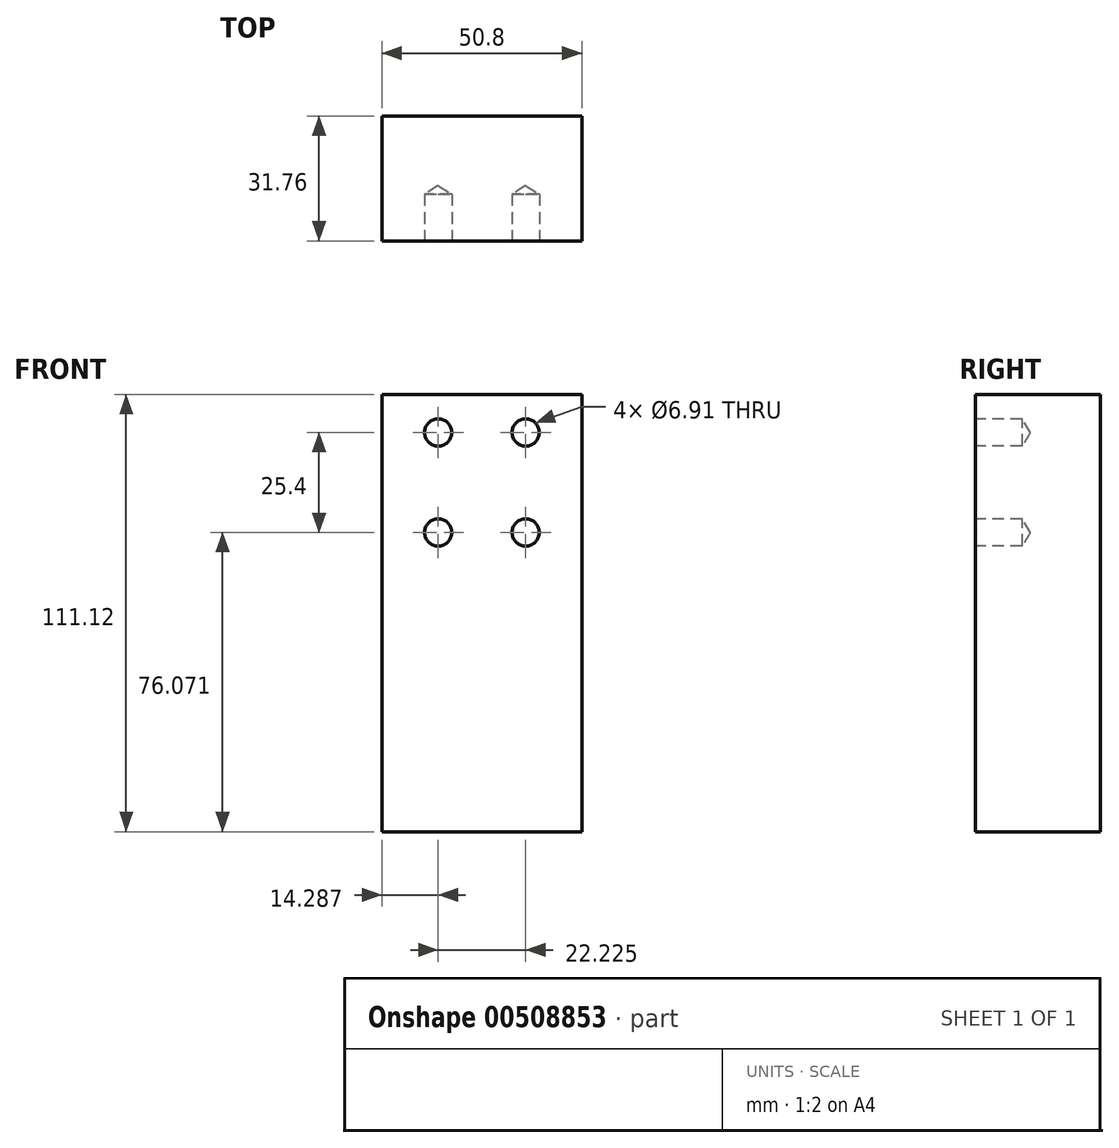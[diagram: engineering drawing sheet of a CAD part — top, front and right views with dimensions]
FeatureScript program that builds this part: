
annotation { "Feature Type Name" : "Feature", "Feature Type Description" : "" }
export const myFeature = defineFeature(function(context is Context, id is Id, definition is map)
    precondition{}
    {
        {
            var Q0;
            Q0=qCreatedBy(makeId("Front.planeOp"),FACE);
            var sketch = newSketch(context, id + "F0", { "sketchPlane" : qUnion([Q0])});
            skLineSegment(sketch, "E0.bottom", {"start": v(25.4, 55.56) * mm, "end": v(-25.4, 55.56) * mm});
            skLineSegment(sketch, "E0.top", {"start": v(25.4, -55.56) * mm, "end": v(-25.4, -55.56) * mm});
            skLineSegment(sketch, "E0.left", {"start": v(25.4, 55.56) * mm, "end": v(25.4, -55.56) * mm});
            skLineSegment(sketch, "E0.right", {"start": v(-25.4, 55.56) * mm, "end": v(-25.4, -55.56) * mm});
            skPoint(sketch, "E0.middle", {"position": v(0, 0) * mm});
            skSolve(sketch);
        }
        {
            var Q0;
            Q0=makeQuery(id+"F0.imprint","IMPRINT",FACE,{"disambiguationData":[TD([[makeQuery(id+"F0.imprint","IMPRINT",EDGE,{"derivedFrom":sQuery(id+"F0.wireOp",EDGE,"E0.bottom")}),1.0]])]});
            extrude(context, id + "F1", {"entities" : qUnion([Q0]), "endBound" : BoundingType.SYMMETRIC, "depth" : 31.75 * mm});
        }
        {
            var Q0;
            Q0=makeQuery(id+"F1.opExtrude","CAP_FACE",FACE,{"disambiguationData":[OSD([sQuery(id+"F0.wireOp",EDGE,"E0.bottom"),sQuery(id+"F0.wireOp",EDGE,"E0.top"),sQuery(id+"F0.wireOp",EDGE,"E0.left"),sQuery(id+"F0.wireOp",EDGE,"E0.right")])],"isStart":false});
            var sketch = newSketch(context, id + "F2", { "sketchPlane" : qUnion([Q0])});
            skPoint(sketch, "E1", {"position": v(-11.11, 45.91) * mm});
            skPoint(sketch, "E2", {"position": v(11.11, 45.91) * mm});
            skPoint(sketch, "E3", {"position": v(-11.11, 20.51) * mm});
            skPoint(sketch, "E4", {"position": v(11.11, 20.51) * mm});
            skSolve(sketch);
        }
        {
            var Q0;
            Q0=sQuery(id+"F2.wireOp",VERTEX,"E1");
            var Q1;
            Q1=sQuery(id+"F2.wireOp",VERTEX,"E2");
            var Q2;
            Q2=sQuery(id+"F2.wireOp",VERTEX,"E3");
            var Q3;
            Q3=sQuery(id+"F2.wireOp",VERTEX,"E4");
            var Q4;
            Q4=makeQuery(id+"F1.opExtrude","SWEPT_BODY",BODY,{"disambiguationData":[OSD([sQuery(id+"F0.wireOp",EDGE,"E0.bottom"),sQuery(id+"F0.wireOp",EDGE,"E0.top"),sQuery(id+"F0.wireOp",EDGE,"E0.left"),sQuery(id+"F0.wireOp",EDGE,"E0.right")])]});
            hole(context, id + "F3", {"style" : HoleStyle.SIMPLE, "endStyle" : HoleEndStyle.BLIND, "standardTappedOrClearance" : lookupTablePath({ "standard" : "ANSI", "engagement" : "75%", "pitch" : "24 tpi", "size" : "5/16", "type" : "Tapped" }), "standardBlindInLast" : lookupTablePath({ "standard" : "ANSI", "engagement" : "75%", "pitch" : "24 tpi", "size" : "5/16", "type" : "Tapped" }), "holeDiameter" : 6.9 * mm, "showTappedDepth" : true, "holeDepth" : 11.94 * mm, "isTappedThrough" : true, "tappedDepth" : 8.76 * mm, "tapClearance" : 3, "locations" : qUnion([Q0, Q1, Q2, Q3]), "scope" : qUnion([Q4]), "majorDiameter" : 7.94 * mm});
        }
    });
